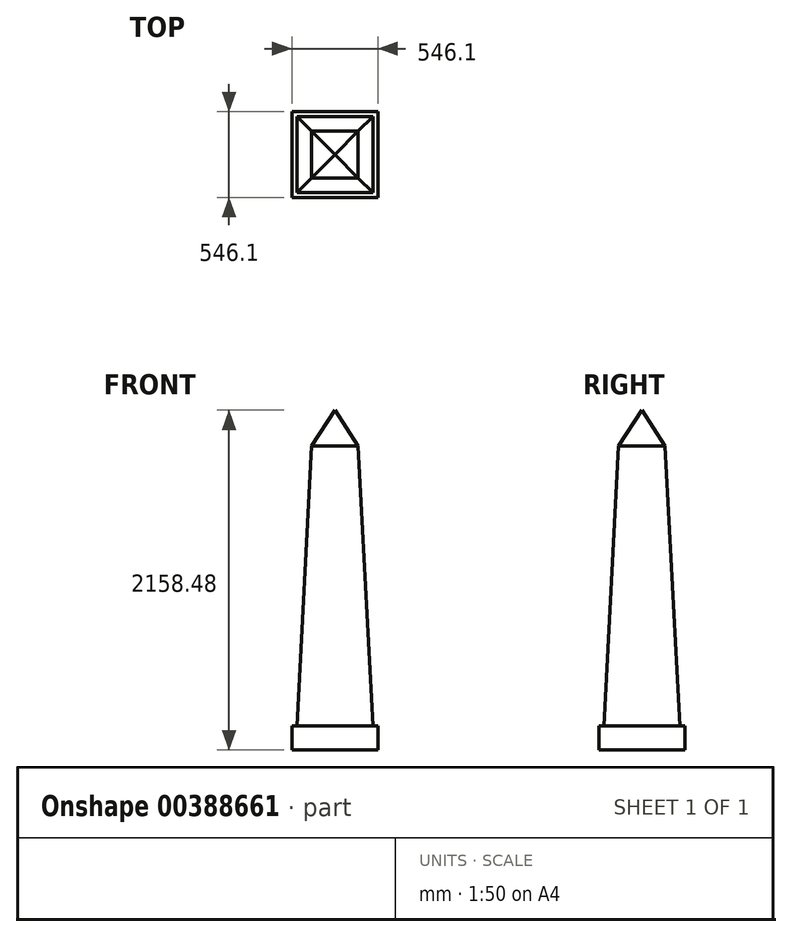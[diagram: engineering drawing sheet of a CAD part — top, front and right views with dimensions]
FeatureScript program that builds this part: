
annotation { "Feature Type Name" : "Feature", "Feature Type Description" : "" }
export const myFeature = defineFeature(function(context is Context, id is Id, definition is map)
    precondition{}
    {
        {
            var Q0;
            Q0=qCreatedBy(makeId("Top.planeOp"),FACE);
            var sketch = newSketch(context, id + "F0", { "sketchPlane" : qUnion([Q0])});
            skLineSegment(sketch, "E0.bottom", {"start": v(-324.58, -215.65) * mm, "end": v(221.52, -215.65) * mm});
            skLineSegment(sketch, "E0.top", {"start": v(-324.58, 330.45) * mm, "end": v(221.52, 330.45) * mm});
            skLineSegment(sketch, "E0.left", {"start": v(-324.58, -215.65) * mm, "end": v(-324.58, 330.45) * mm});
            skLineSegment(sketch, "E0.right", {"start": v(221.52, -215.65) * mm, "end": v(221.52, 330.45) * mm});
            skSolve(sketch);
        }
        {
            var Q0;
            Q0 = qSketchRegion(id + "F0", true);
            extrude(context, id + "F1", {"entities" : qUnion([Q0]), "depth" : 152.4 * mm});
        }
        {
            var Q0;
            Q0=makeQuery(id+"F1.opExtrude","CAP_FACE",FACE,{"disambiguationData":[OSD([sQuery(id+"F0.wireOp",EDGE,"E0.bottom"),sQuery(id+"F0.wireOp",EDGE,"E0.top"),sQuery(id+"F0.wireOp",EDGE,"E0.left"),sQuery(id+"F0.wireOp",EDGE,"E0.right")])],"isStart":false});
            var sketch = newSketch(context, id + "F2", { "sketchPlane" : qUnion([Q0])});
            skLineSegment(sketch, "E1.bottom", {"start": v(-292.83, -183.9) * mm, "end": v(189.77, -183.9) * mm});
            skLineSegment(sketch, "E1.top", {"start": v(-292.83, 298.7) * mm, "end": v(189.77, 298.7) * mm});
            skLineSegment(sketch, "E1.left", {"start": v(-292.83, -183.9) * mm, "end": v(-292.83, 298.7) * mm});
            skLineSegment(sketch, "E1.right", {"start": v(189.77, -183.9) * mm, "end": v(189.77, 298.7) * mm});
            skPoint(sketch, "E1.middle", {"position": v(-51.53, 57.4) * mm});
            skPoint(sketch, "E1.middle.positionSnap0", {"position": v(-324.58, 57.4) * mm});
            skPoint(sketch, "E1.middle.positionSnap1", {"position": v(-51.53, -215.65) * mm});
            skPoint(sketch, "E1.centerSnap0", {"position": v(-324.58, 57.4) * mm});
            skPoint(sketch, "E1.centerSnap1", {"position": v(-51.53, -215.65) * mm});
            skSolve(sketch);
        }
        {
            var Q0;
            Q0 = qSketchRegion(id + "F2", true);
            extrude(context, id + "F3", {"entities" : qUnion([Q0]), "operationType" : NewBodyOperationType.ADD, "depth" : 1778 * mm, "hasDraft" : true, "draftAngle" : 3 * degree, "draftPullDirection" : true});
        }
        {
            var Q0;
            Q0=makeQuery(id+"F3.opExtrude","CAP_FACE",FACE,{"disambiguationData":[OSD([sQuery(id+"F2.wireOp",EDGE,"E1.bottom"),sQuery(id+"F2.wireOp",EDGE,"E1.top"),sQuery(id+"F2.wireOp",EDGE,"E1.left"),sQuery(id+"F2.wireOp",EDGE,"E1.right")])],"isStart":false});
            var sketch = newSketch(context, id + "F4", { "sketchPlane" : qUnion([Q0])});
            skLineSegment(sketch, "E2.bottom", {"start": v(96.59, 205.52) * mm, "end": v(-199.65, 205.52) * mm});
            skLineSegment(sketch, "E2.top", {"start": v(96.59, -90.72) * mm, "end": v(-199.65, -90.72) * mm});
            skLineSegment(sketch, "E2.left", {"start": v(96.59, 205.52) * mm, "end": v(96.59, -90.72) * mm});
            skLineSegment(sketch, "E2.right", {"start": v(-199.65, 205.52) * mm, "end": v(-199.65, -90.72) * mm});
            skPoint(sketch, "E2.middle", {"position": v(-51.53, 57.4) * mm});
            skPoint(sketch, "E2.middle.positionSnap0", {"position": v(-51.53, 205.52) * mm});
            skPoint(sketch, "E2.middle.positionSnap1", {"position": v(-199.65, 57.4) * mm});
            skPoint(sketch, "E2.centerSnap0", {"position": v(-51.53, 205.52) * mm});
            skPoint(sketch, "E2.centerSnap1", {"position": v(-199.65, 57.4) * mm});
            skSolve(sketch);
        }
        {
            var Q0;
            Q0 = qSketchRegion(id + "F4", true);
            extrude(context, id + "F5", {"entities" : qUnion([Q0]), "operationType" : NewBodyOperationType.ADD, "depth" : 241.3 * mm, "hasDraft" : true, "draftAngle" : 33 * degree, "draftPullDirection" : true});
        }
    });
